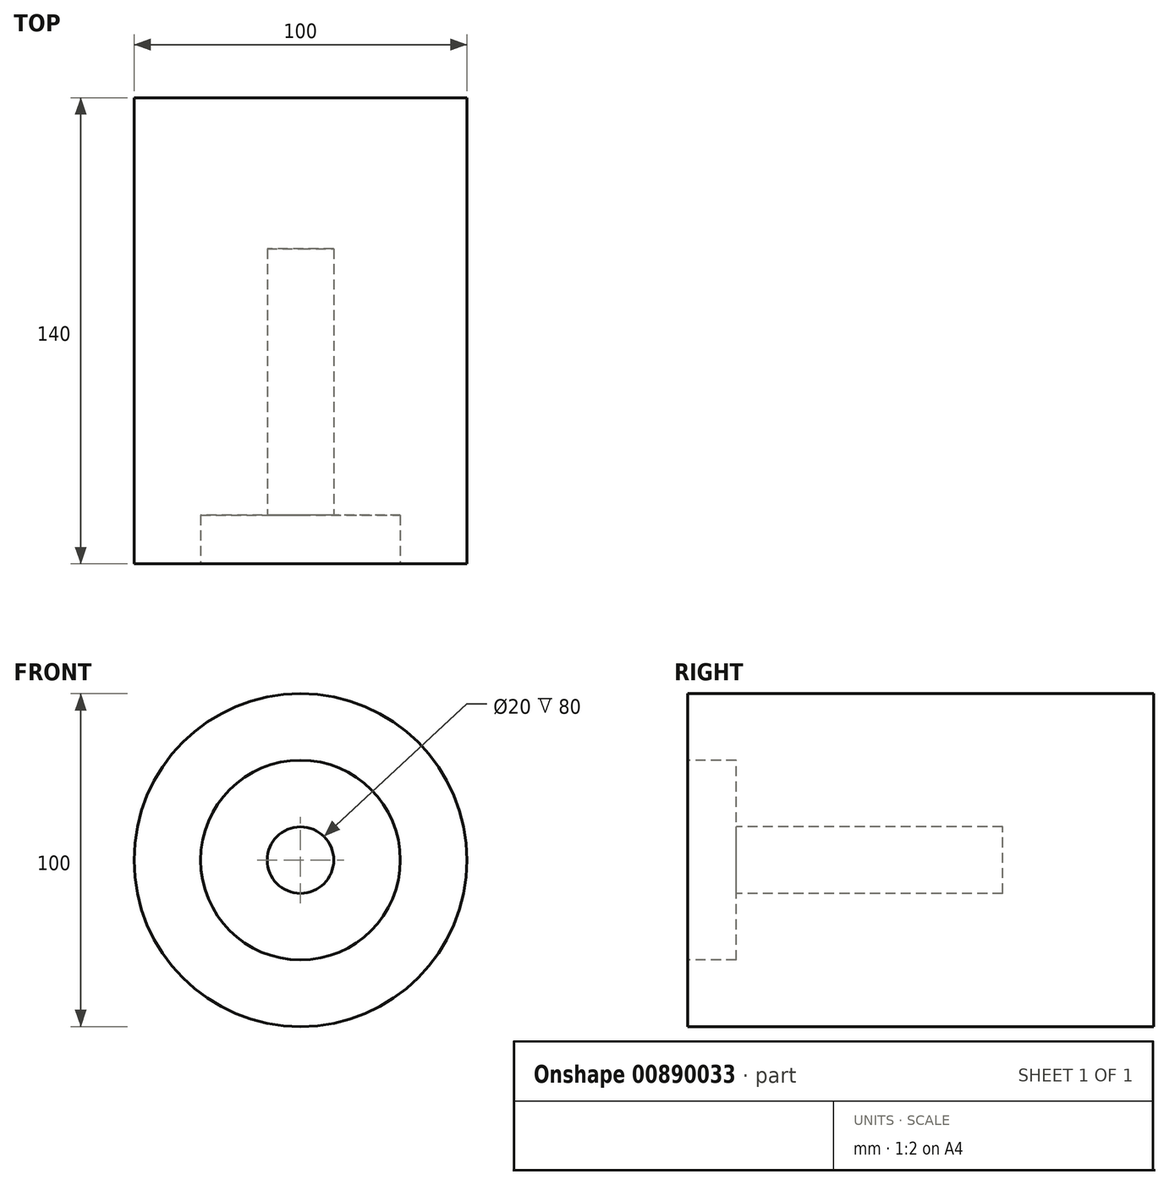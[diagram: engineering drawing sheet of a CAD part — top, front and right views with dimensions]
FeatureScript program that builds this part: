
annotation { "Feature Type Name" : "Feature", "Feature Type Description" : "" }
export const myFeature = defineFeature(function(context is Context, id is Id, definition is map)
    precondition{}
    {
        {
            var Q0;
            Q0=qCreatedBy(makeId("Front.planeOp"),FACE);
            var sketch = newSketch(context, id + "F0", { "sketchPlane" : qUnion([Q0])});
            skCircle(sketch, "E0", {"center": v(0, 0) * mm, "radius": 50 * mm});
            skSolve(sketch);
        }
        {
            var Q0;
            Q0=makeQuery(id+"F0.imprint","IMPRINT",FACE,{"disambiguationData":[TD([[makeQuery(id+"F0.imprint","IMPRINT",EDGE,{"derivedFrom":sQuery(id+"F0.wireOp",EDGE,"E0")}),1.0]])]});
            extrude(context, id + "F1", {"entities" : qUnion([Q0]), "depth" : 70 * mm, "offsetDistance" : 25.4 * mm});
        }
        {
            var Q0;
            Q0=makeQuery(id+"F1.opExtrude","CAP_FACE",FACE,{"disambiguationData":[OSD([sQuery(id+"F0.wireOp",EDGE,"E0")])],"isStart":true});
            extrude(context, id + "F2", {"entities" : qUnion([Q0]), "operationType" : NewBodyOperationType.ADD, "depth" : 70 * mm, "offsetDistance" : 25.4 * mm});
        }
        {
            var Q0;
            Q0=makeQuery(id+"F1.opExtrude","CAP_FACE",FACE,{"disambiguationData":[OSD([sQuery(id+"F0.wireOp",EDGE,"E0")])],"isStart":false});
            var sketch = newSketch(context, id + "F3", { "sketchPlane" : qUnion([Q0])});
            skCircle(sketch, "E1", {"center": v(0, 0) * mm, "radius": 30 * mm});
            skSolve(sketch);
        }
        {
            var Q0;
            Q0 = qSketchRegion(id + "F3", true);
            extrude(context, id + "F4", {"entities" : qUnion([Q0]), "operationType" : NewBodyOperationType.REMOVE, "oppositeDirection" : true, "depth" : 40 * mm, "offsetDistance" : 25.4 * mm});
        }
        {
            var Q0;
            Q0=makeQuery(id+"F4.boolean.opBoolean","COPY",FACE,{"derivedFrom":makeQuery(id+"F4.opExtrude","CAP_FACE",FACE,{"disambiguationData":[OSD([sQuery(id+"F3.wireOp",EDGE,"E1")])],"isStart":false})});
            var sketch = newSketch(context, id + "F5", { "sketchPlane" : qUnion([Q0])});
            skSolve(sketch);
        }
        {
            var Q0;
            Q0=makeQuery(id+"F5.imprint","IMPRINT",FACE,{"disambiguationData":[TD([[makeQuery(id+"F5.imprint","IMPRINT",EDGE,{"derivedFrom":makeQuery(id+"F4.boolean.opBoolean","COPY",EDGE,{"derivedFrom":makeQuery(id+"F4.opExtrude","CAP_EDGE",EDGE,{"disambiguationData":[OSD([sQuery(id+"F3.wireOp",EDGE,"E1")])],"isStart":false})})}),1.0]])]});
            extrude(context, id + "F6", {"entities" : qUnion([Q0]), "operationType" : NewBodyOperationType.ADD, "depth" : 25.4 * mm, "offsetDistance" : 25.4 * mm});
        }
        {
            var Q0;
            Q0=makeQuery(id+"F6.opExtrude","CAP_FACE",FACE,{"disambiguationData":[OSD([sQuery(id+"F3.wireOp",EDGE,"E1")])],"isStart":false});
            var sketch = newSketch(context, id + "F7", { "sketchPlane" : qUnion([Q0])});
            skCircle(sketch, "E2", {"center": v(0, 0) * mm, "radius": 10 * mm});
            skSolve(sketch);
        }
        {
            var Q0;
            Q0=makeQuery(id+"F7.imprint","IMPRINT",FACE,{"disambiguationData":[TD([[makeQuery(id+"F7.imprint","IMPRINT",EDGE,{"derivedFrom":sQuery(id+"F7.wireOp",EDGE,"E2")}),1.0]])]});
            extrude(context, id + "F8", {"entities" : qUnion([Q0]), "operationType" : NewBodyOperationType.REMOVE, "oppositeDirection" : true, "depth" : 80 * mm, "offsetDistance" : 25.4 * mm});
        }
    });
